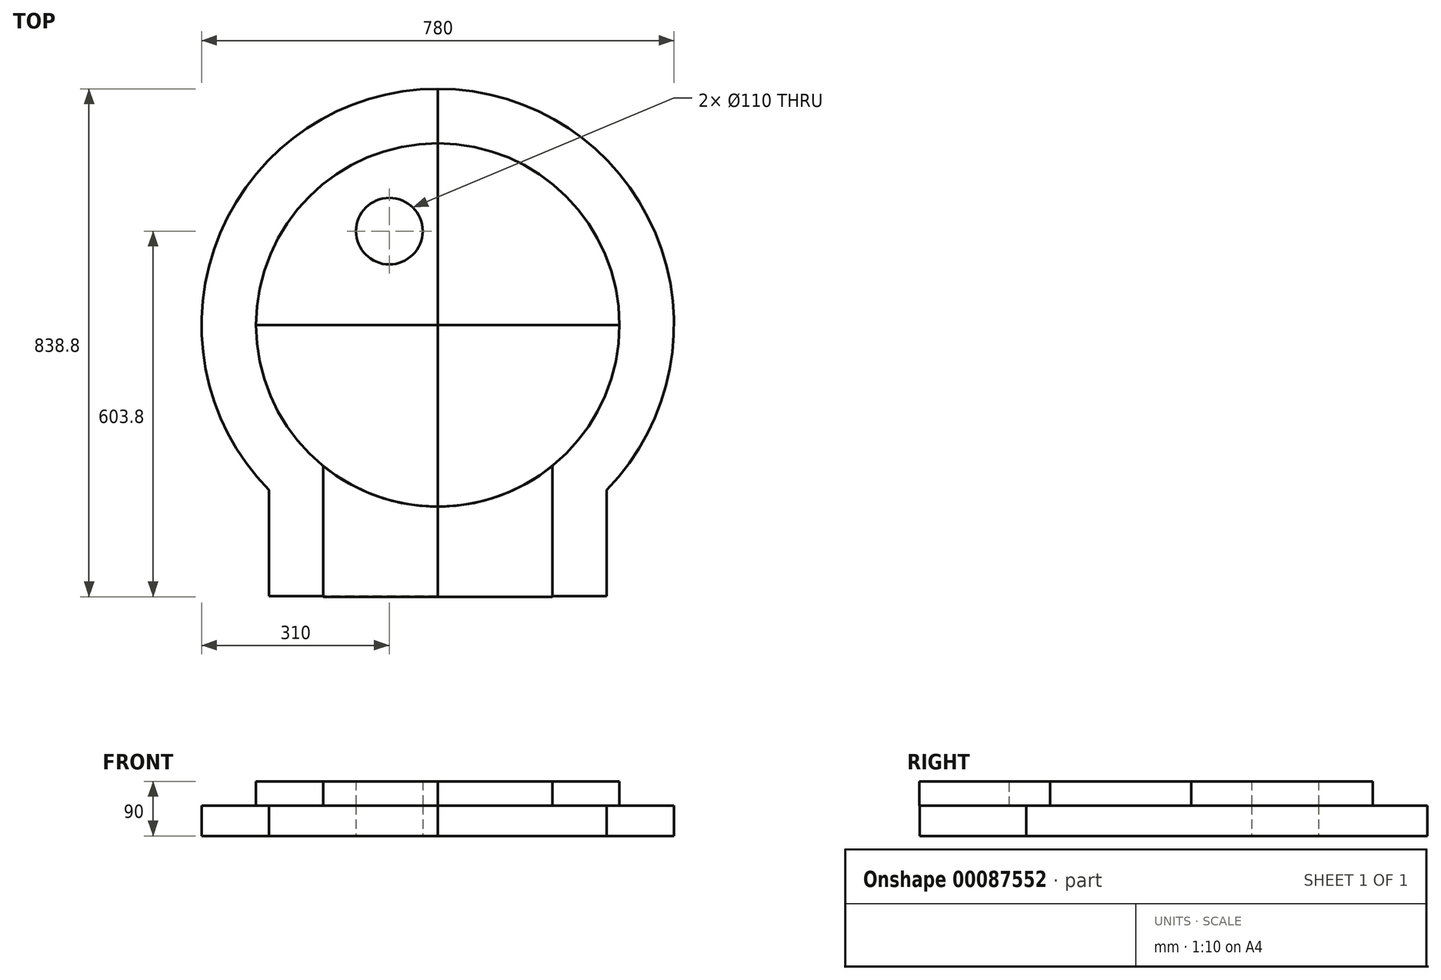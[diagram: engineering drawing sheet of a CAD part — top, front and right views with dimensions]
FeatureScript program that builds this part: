
annotation { "Feature Type Name" : "Feature", "Feature Type Description" : "" }
export const myFeature = defineFeature(function(context is Context, id is Id, definition is map)
    precondition{}
    {
        {
            var Q0;
            Q0=qCreatedBy(makeId("Front.planeOp"),FACE);
            var sketch = newSketch(context, id + "F0", { "sketchPlane" : qUnion([Q0])});
            skLineSegment(sketch, "E0", {"start": v(0, 0) * mm, "end": v(300, 0) * mm});
            skLineSegment(sketch, "E1", {"start": v(0, 0) * mm, "end": v(0, 40) * mm});
            skLineSegment(sketch, "E2", {"start": v(300, 0) * mm, "end": v(300, 40) * mm});
            skLineSegment(sketch, "E3", {"start": v(0, 40) * mm, "end": v(300, 40) * mm});
            skSolve(sketch);
        }
        {
            var Q0;
            Q0=makeQuery(id+"F0.imprint","IMPRINT",FACE,{"disambiguationData":[TD([[makeQuery(id+"F0.imprint","IMPRINT",EDGE,{"derivedFrom":sQuery(id+"F0.wireOp",EDGE,"E0")}),1.0]])]});
            var Q1;
            Q1=sQuery(id+"F0.wireOp",EDGE,"E1");
            revolve(context, id + "F1", {"entities" : qUnion([Q0]), "axis" : qUnion([Q1]), "revolveType" : RevolveType.ONE_DIRECTION, "angle" : 90 * degree});
        }
        {
            var Q0;
            Q0=makeQuery(id+"F1.opRevolve","SWEPT_BODY",BODY,{"disambiguationData":[OSD([sQuery(id+"F0.wireOp",EDGE,"E0"),sQuery(id+"F0.wireOp",EDGE,"E1"),sQuery(id+"F0.wireOp",EDGE,"E2"),sQuery(id+"F0.wireOp",EDGE,"E3")])]});
            var Q1;
            Q1=makeQuery(id+"F1.opRevolve","CAP_EDGE",EDGE,{"disambiguationData":[OSD([sQuery(id+"F0.wireOp",EDGE,"E1")])],"isStart":true});
            transform(context, id + "F2", {"entities" : qUnion([Q0]), "transformType" : TransformType.ROTATION, "transformAxis" : qUnion([Q1]), "angle" : 90 * degree, "makeCopy" : true});
        }
        {
            var Q0;
            Q0=makeQuery(id+"F2.opPattern","COPY",BODY,{"derivedFrom":makeQuery(id+"F1.opRevolve","SWEPT_BODY",BODY,{"disambiguationData":[OSD([sQuery(id+"F0.wireOp",EDGE,"E0"),sQuery(id+"F0.wireOp",EDGE,"E1"),sQuery(id+"F0.wireOp",EDGE,"E2"),sQuery(id+"F0.wireOp",EDGE,"E3")])]}),"instanceName":"1"});
            var Q1;
            Q1=makeQuery(id+"F1.opRevolve","CAP_EDGE",EDGE,{"disambiguationData":[OSD([sQuery(id+"F0.wireOp",EDGE,"E1")])],"isStart":true});
            transform(context, id + "F3", {"entities" : qUnion([Q0]), "transformType" : TransformType.ROTATION, "transformAxis" : qUnion([Q1]), "angle" : 90 * degree, "makeCopy" : true});
        }
        {
            var Q0;
            Q0=makeQuery(id+"F3.opPattern","COPY",BODY,{"derivedFrom":makeQuery(id+"F2.opPattern","COPY",BODY,{"derivedFrom":makeQuery(id+"F1.opRevolve","SWEPT_BODY",BODY,{"disambiguationData":[OSD([sQuery(id+"F0.wireOp",EDGE,"E0"),sQuery(id+"F0.wireOp",EDGE,"E1"),sQuery(id+"F0.wireOp",EDGE,"E2"),sQuery(id+"F0.wireOp",EDGE,"E3")])]}),"instanceName":"1"}),"instanceName":"1"});
            var Q1;
            Q1=makeQuery(id+"F1.opRevolve","CAP_EDGE",EDGE,{"disambiguationData":[OSD([sQuery(id+"F0.wireOp",EDGE,"E1")])],"isStart":true});
            transform(context, id + "F4", {"entities" : qUnion([Q0]), "transformType" : TransformType.ROTATION, "transformAxis" : qUnion([Q1]), "angle" : 90 * degree, "makeCopy" : true});
        }
        {
            var Q0;
            Q0=qCreatedBy(makeId("Right.planeOp"),FACE);
            var sketch = newSketch(context, id + "F5", { "sketchPlane" : qUnion([Q0])});
            skLineSegment(sketch, "E4", {"start": v(0, 0) * mm, "end": v(300, 0) * mm});
            skLineSegment(sketch, "E5", {"start": v(0, 0) * mm, "end": v(0, 40) * mm});
            skLineSegment(sketch, "E6", {"start": v(300, 0) * mm, "end": v(300, 40) * mm});
            skLineSegment(sketch, "E7", {"start": v(0, 40) * mm, "end": v(300, 40) * mm});
            skSolve(sketch);
        }
        {
            var Q0;
            Q0=makeQuery(id+"F5.imprint","IMPRINT",FACE,{"disambiguationData":[TD([[makeQuery(id+"F5.imprint","IMPRINT",EDGE,{"derivedFrom":sQuery(id+"F5.wireOp",EDGE,"E4")}),1.0]])]});
            extrude(context, id + "F6", {"entities" : qUnion([Q0]), "depth" : 189 * mm});
        }
        {
            var Q0;
            Q0=makeQuery(id+"F6.opExtrude","SWEPT_BODY",BODY,{"disambiguationData":[OSD([sQuery(id+"F5.wireOp",EDGE,"E4"),sQuery(id+"F5.wireOp",EDGE,"E5"),sQuery(id+"F5.wireOp",EDGE,"E6"),sQuery(id+"F5.wireOp",EDGE,"E7")])]});
            transform(context, id + "F7", {"entities" : qUnion([Q0]), "transformType" : TransformType.TRANSLATION_3D, "dx" : 0 * mm, "dy" : -448.8 * mm, "dz" : 0 * mm, "makeCopy" : false});
        }
        {
            var Q0;
            Q0=makeQuery(id+"F6.opExtrude","SWEPT_BODY",BODY,{"disambiguationData":[OSD([sQuery(id+"F5.wireOp",EDGE,"E4"),sQuery(id+"F5.wireOp",EDGE,"E5"),sQuery(id+"F5.wireOp",EDGE,"E6"),sQuery(id+"F5.wireOp",EDGE,"E7")])]});
            transform(context, id + "F8", {"entities" : qUnion([Q0]), "transformType" : TransformType.TRANSLATION_3D, "dx" : -189 * mm, "dy" : 0 * mm, "dz" : 0 * mm, "makeCopy" : true});
        }
        {
            var Q0;
            Q0=makeQuery(id+"F3.opPattern","COPY",BODY,{"derivedFrom":makeQuery(id+"F2.opPattern","COPY",BODY,{"derivedFrom":makeQuery(id+"F1.opRevolve","SWEPT_BODY",BODY,{"disambiguationData":[OSD([sQuery(id+"F0.wireOp",EDGE,"E0"),sQuery(id+"F0.wireOp",EDGE,"E1"),sQuery(id+"F0.wireOp",EDGE,"E2"),sQuery(id+"F0.wireOp",EDGE,"E3")])]}),"instanceName":"1"}),"instanceName":"1"});
            var Q1;
            Q1=makeQuery(id+"F8.opPattern","COPY",BODY,{"derivedFrom":makeQuery(id+"F6.opExtrude","SWEPT_BODY",BODY,{"disambiguationData":[OSD([sQuery(id+"F5.wireOp",EDGE,"E4"),sQuery(id+"F5.wireOp",EDGE,"E5"),sQuery(id+"F5.wireOp",EDGE,"E6"),sQuery(id+"F5.wireOp",EDGE,"E7")])]}),"instanceName":"1"});
            booleanBodies(context, id + "F9", {"operationType" : BooleanOperationType.SUBTRACTION, "tools" : qUnion([Q0]), "targets" : qUnion([Q1]), "keepTools" : true});
        }
        {
            var Q0;
            Q0=makeQuery(id+"F4.opPattern","COPY",BODY,{"derivedFrom":makeQuery(id+"F3.opPattern","COPY",BODY,{"derivedFrom":makeQuery(id+"F2.opPattern","COPY",BODY,{"derivedFrom":makeQuery(id+"F1.opRevolve","SWEPT_BODY",BODY,{"disambiguationData":[OSD([sQuery(id+"F0.wireOp",EDGE,"E0"),sQuery(id+"F0.wireOp",EDGE,"E1"),sQuery(id+"F0.wireOp",EDGE,"E2"),sQuery(id+"F0.wireOp",EDGE,"E3")])]}),"instanceName":"1"}),"instanceName":"1"}),"instanceName":"1"});
            var Q1;
            Q1=makeQuery(id+"F6.opExtrude","SWEPT_BODY",BODY,{"disambiguationData":[OSD([sQuery(id+"F5.wireOp",EDGE,"E4"),sQuery(id+"F5.wireOp",EDGE,"E5"),sQuery(id+"F5.wireOp",EDGE,"E6"),sQuery(id+"F5.wireOp",EDGE,"E7")])]});
            booleanBodies(context, id + "F10", {"operationType" : BooleanOperationType.SUBTRACTION, "tools" : qUnion([Q0]), "targets" : qUnion([Q1]), "keepTools" : true});
        }
        {
            var Q0;
            Q0=qCreatedBy(makeId("Top.planeOp"),FACE);
            var sketch = newSketch(context, id + "F11", { "sketchPlane" : qUnion([Q0])});
            skLineSegment(sketch, "E8", {"start": v(0, 0) * mm, "end": v(410, 0) * mm});
            skLineSegment(sketch, "E9", {"start": v(410, 0) * mm, "end": v(410, 450) * mm});
            skLineSegment(sketch, "E10", {"start": v(0, 0) * mm, "end": v(-410, 0) * mm});
            skLineSegment(sketch, "E11", {"start": v(-410, 0) * mm, "end": v(-410, -410) * mm});
            skLineSegment(sketch, "E12", {"start": v(0, 0) * mm, "end": v(0, -410) * mm});
            skLineSegment(sketch, "E13", {"start": v(0, 0) * mm, "end": v(0, 450) * mm});
            skLineSegment(sketch, "E14.bottom", {"start": v(-410, -410) * mm, "end": v(0, -410) * mm});
            skLineSegment(sketch, "E14.top", {"start": v(-410, 450) * mm, "end": v(0, 450) * mm});
            skLineSegment(sketch, "E14.right", {"start": v(0, -410) * mm, "end": v(0, 450) * mm});
            skLineSegment(sketch, "E15.bottom", {"start": v(0, -410) * mm, "end": v(410, -410) * mm});
            skLineSegment(sketch, "E15.top", {"start": v(0, 450) * mm, "end": v(410, 450) * mm});
            skLineSegment(sketch, "E16", {"start": v(-410, 0) * mm, "end": v(-410, 450) * mm});
            skLineSegment(sketch, "E17", {"start": v(410, 0) * mm, "end": v(410, -410) * mm});
            skSolve(sketch);
        }
        {
            var Q0;
            {var subQ0=sQuery(id+"F11.wireOp",EDGE,"E8");Q0=makeQuery(id+"F11.imprint","IMPRINT",FACE,{"disambiguationData":[TD([[makeQuery(id+"F11.imprint","IMPRINT",EDGE,{"derivedFrom":subQ0}),-1.0]])]});}
            var Q1;
            {var subQ0=sQuery(id+"F11.wireOp",EDGE,"E8");Q1=makeQuery(id+"F11.imprint","IMPRINT",FACE,{"disambiguationData":[TD([[makeQuery(id+"F11.imprint","IMPRINT",EDGE,{"derivedFrom":subQ0}),1.0]])]});}
            var Q2;
            {var subQ0=sQuery(id+"F11.wireOp",EDGE,"E10");Q2=makeQuery(id+"F11.imprint","IMPRINT",FACE,{"disambiguationData":[TD([[makeQuery(id+"F11.imprint","IMPRINT",EDGE,{"derivedFrom":subQ0}),-1.0]])]});}
            var Q3;
            {var subQ0=sQuery(id+"F11.wireOp",EDGE,"E10");Q3=makeQuery(id+"F11.imprint","IMPRINT",FACE,{"disambiguationData":[TD([[makeQuery(id+"F11.imprint","IMPRINT",EDGE,{"derivedFrom":subQ0}),1.0]])]});}
            extrude(context, id + "F12", {"entities" : qUnion([Q0, Q1, Q2, Q3]), "depth" : 50 * mm});
        }
        {
            var Q0;
            Q0=makeQuery(id+"F12.opExtrude","SWEPT_BODY",BODY,{"disambiguationData":[OSD([sQuery(id+"F11.wireOp",EDGE,"E14.bottom"),sQuery(id+"F11.wireOp",EDGE,"E14.top"),sQuery(id+"F11.wireOp",EDGE,"E14.left"),sQuery(id+"F11.wireOp",EDGE,"E15.bottom"),sQuery(id+"F11.wireOp",EDGE,"E15.top"),sQuery(id+"F11.wireOp",EDGE,"E15.right")])]});
            transform(context, id + "F13", {"entities" : qUnion([Q0]), "transformType" : TransformType.TRANSLATION_3D, "dx" : 0 * mm, "dy" : 0 * mm, "dz" : -50 * mm, "makeCopy" : false});
        }
        {
            var Q0;
            Q0=makeQuery(id+"F12.opExtrude","SWEPT_BODY",BODY,{"disambiguationData":[OSD([sQuery(id+"F11.wireOp",EDGE,"E9"),sQuery(id+"F11.wireOp",EDGE,"E11"),sQuery(id+"F11.wireOp",EDGE,"E14.bottom"),sQuery(id+"F11.wireOp",EDGE,"E14.top"),sQuery(id+"F11.wireOp",EDGE,"E15.bottom"),sQuery(id+"F11.wireOp",EDGE,"E15.top"),sQuery(id+"F11.wireOp",EDGE,"E16"),sQuery(id+"F11.wireOp",EDGE,"E17")])]});
            transform(context, id + "F14", {"entities" : qUnion([Q0]), "transformType" : TransformType.TRANSLATION_3D, "dx" : 0 * mm, "dy" : -40 * mm, "dz" : 0 * mm, "makeCopy" : false});
        }
        {
            var Q0;
            Q0=makeQuery(id+"F3.opPattern","COPY",BODY,{"derivedFrom":makeQuery(id+"F2.opPattern","COPY",BODY,{"derivedFrom":makeQuery(id+"F1.opRevolve","SWEPT_BODY",BODY,{"disambiguationData":[OSD([sQuery(id+"F0.wireOp",EDGE,"E0"),sQuery(id+"F0.wireOp",EDGE,"E1"),sQuery(id+"F0.wireOp",EDGE,"E2"),sQuery(id+"F0.wireOp",EDGE,"E3")])]}),"instanceName":"1"}),"instanceName":"1"});
            var Q1;
            Q1=makeQuery(id+"F2.opPattern","COPY",BODY,{"derivedFrom":makeQuery(id+"F1.opRevolve","SWEPT_BODY",BODY,{"disambiguationData":[OSD([sQuery(id+"F0.wireOp",EDGE,"E0"),sQuery(id+"F0.wireOp",EDGE,"E1"),sQuery(id+"F0.wireOp",EDGE,"E2"),sQuery(id+"F0.wireOp",EDGE,"E3")])]}),"instanceName":"1"});
            var Q2;
            Q2=makeQuery(id+"F4.opPattern","COPY",BODY,{"derivedFrom":makeQuery(id+"F3.opPattern","COPY",BODY,{"derivedFrom":makeQuery(id+"F2.opPattern","COPY",BODY,{"derivedFrom":makeQuery(id+"F1.opRevolve","SWEPT_BODY",BODY,{"disambiguationData":[OSD([sQuery(id+"F0.wireOp",EDGE,"E0"),sQuery(id+"F0.wireOp",EDGE,"E1"),sQuery(id+"F0.wireOp",EDGE,"E2"),sQuery(id+"F0.wireOp",EDGE,"E3")])]}),"instanceName":"1"}),"instanceName":"1"}),"instanceName":"1"});
            var Q3;
            Q3=makeQuery(id+"F6.opExtrude","SWEPT_BODY",BODY,{"disambiguationData":[OSD([sQuery(id+"F5.wireOp",EDGE,"E4"),sQuery(id+"F5.wireOp",EDGE,"E5"),sQuery(id+"F5.wireOp",EDGE,"E6"),sQuery(id+"F5.wireOp",EDGE,"E7")])]});
            var Q4;
            Q4=makeQuery(id+"F8.opPattern","COPY",BODY,{"derivedFrom":makeQuery(id+"F6.opExtrude","SWEPT_BODY",BODY,{"disambiguationData":[OSD([sQuery(id+"F5.wireOp",EDGE,"E4"),sQuery(id+"F5.wireOp",EDGE,"E5"),sQuery(id+"F5.wireOp",EDGE,"E6"),sQuery(id+"F5.wireOp",EDGE,"E7")])]}),"instanceName":"1"});
            var Q5;
            Q5=makeQuery(id+"F12.opExtrude","SWEPT_BODY",BODY,{"disambiguationData":[OSD([sQuery(id+"F11.wireOp",EDGE,"E9"),sQuery(id+"F11.wireOp",EDGE,"E11"),sQuery(id+"F11.wireOp",EDGE,"E14.bottom"),sQuery(id+"F11.wireOp",EDGE,"E14.top"),sQuery(id+"F11.wireOp",EDGE,"E15.bottom"),sQuery(id+"F11.wireOp",EDGE,"E15.top"),sQuery(id+"F11.wireOp",EDGE,"E16"),sQuery(id+"F11.wireOp",EDGE,"E17")])]});
            var Q6;
            Q6=makeQuery(id+"F1.opRevolve","SWEPT_BODY",BODY,{"disambiguationData":[OSD([sQuery(id+"F0.wireOp",EDGE,"E0"),sQuery(id+"F0.wireOp",EDGE,"E1"),sQuery(id+"F0.wireOp",EDGE,"E2"),sQuery(id+"F0.wireOp",EDGE,"E3")])]});
            transform(context, id + "F15", {"entities" : qUnion([Q0, Q1, Q2, Q3, Q4, Q5, Q6]), "transformType" : TransformType.TRANSLATION_3D, "dx" : 0 * mm, "dy" : 20 * mm, "dz" : -50 * mm, "makeCopy" : false});
        }
        {
            var Q0;
            Q0=qCreatedBy(makeId("Top.planeOp"),FACE);
            var sketch = newSketch(context, id + "F16", { "sketchPlane" : qUnion([Q0])});
            skLineSegment(sketch, "E18", {"start": v(0, 0) * mm, "end": v(0, 20) * mm});
            skLineSegment(sketch, "E19", {"start": v(0, 20) * mm, "end": v(0, 410) * mm});
            skLineSegment(sketch, "E20", {"start": v(0, 20) * mm, "end": v(0, -428) * mm});
            skLineSegment(sketch, "E21", {"start": v(0, -428) * mm, "end": v(-279, -428) * mm});
            skLineSegment(sketch, "E22", {"start": v(-279, -428) * mm, "end": v(-279, -252.5) * mm});
            skArc(sketch, "E23", {"start": v(-279, -252.5) * mm, "mid": v(-359.43, 171.37) * mm, "end": v(0, 410) * mm});
            skSolve(sketch);
        }
        {
            var Q0;
            {var subQ1=sQuery(id+"F16.wireOp",EDGE,"E19");Q0=makeQuery(id+"F16.imprint","IMPRINT",FACE,{"disambiguationData":[TD([[makeQuery(id+"F16.imprint","IMPRINT",EDGE,{"derivedFrom":subQ1}),1.0]])]});}
            extrude(context, id + "F17", {"entities" : qUnion([Q0]), "depth" : 50 * mm});
        }
        {
            var Q0;
            Q0=makeQuery(id+"F17.opExtrude","SWEPT_BODY",BODY,{"disambiguationData":[OSD([sQuery(id+"F16.wireOp",EDGE,"E19"),sQuery(id+"F16.wireOp",EDGE,"E20"),sQuery(id+"F16.wireOp",EDGE,"E21"),sQuery(id+"F16.wireOp",EDGE,"E22"),sQuery(id+"F16.wireOp",EDGE,"E23")])]});
            transform(context, id + "F18", {"entities" : qUnion([Q0]), "transformType" : TransformType.TRANSLATION_3D, "dx" : 0 * mm, "dy" : 0 * mm, "dz" : -100 * mm, "makeCopy" : false});
        }
        {
            var Q0;
            Q0=makeQuery(id+"F17.opExtrude","SWEPT_BODY",BODY,{"disambiguationData":[OSD([sQuery(id+"F16.wireOp",EDGE,"E19"),sQuery(id+"F16.wireOp",EDGE,"E20"),sQuery(id+"F16.wireOp",EDGE,"E21"),sQuery(id+"F16.wireOp",EDGE,"E22"),sQuery(id+"F16.wireOp",EDGE,"E23")])]});
            var Q1;
            Q1=makeQuery(id+"F17.opExtrude","CAP_EDGE",EDGE,{"disambiguationData":[OSD([sQuery(id+"F16.wireOp",EDGE,"E19"),sQuery(id+"F16.wireOp",EDGE,"E20")])],"isStart":false});
            transform(context, id + "F19", {"entities" : qUnion([Q0]), "transformType" : TransformType.ROTATION, "transformAxis" : qUnion([Q1]), "angle" : 180 * degree, "makeCopy" : true});
        }
        {
            var Q0;
            Q0=makeQuery(id+"F19.opPattern","COPY",BODY,{"derivedFrom":makeQuery(id+"F17.opExtrude","SWEPT_BODY",BODY,{"disambiguationData":[OSD([sQuery(id+"F16.wireOp",EDGE,"E19"),sQuery(id+"F16.wireOp",EDGE,"E20"),sQuery(id+"F16.wireOp",EDGE,"E21"),sQuery(id+"F16.wireOp",EDGE,"E22"),sQuery(id+"F16.wireOp",EDGE,"E23")])]}),"instanceName":"1"});
            transform(context, id + "F20", {"entities" : qUnion([Q0]), "transformType" : TransformType.TRANSLATION_3D, "dx" : 0 * mm, "dy" : 0 * mm, "dz" : -50 * mm, "makeCopy" : false});
        }
        {
            var Q0;
            Q0=makeQuery(id+"F12.opExtrude","SWEPT_BODY",BODY,{"disambiguationData":[OSD([sQuery(id+"F11.wireOp",EDGE,"E9"),sQuery(id+"F11.wireOp",EDGE,"E11"),sQuery(id+"F11.wireOp",EDGE,"E14.bottom"),sQuery(id+"F11.wireOp",EDGE,"E14.top"),sQuery(id+"F11.wireOp",EDGE,"E15.bottom"),sQuery(id+"F11.wireOp",EDGE,"E15.top"),sQuery(id+"F11.wireOp",EDGE,"E16"),sQuery(id+"F11.wireOp",EDGE,"E17")])]});
            deleteBodies(context, id + "F21", {"entities" : qUnion([Q0])});
        }
        {
            var Q0;
            Q0=qCreatedBy(makeId("Top.planeOp"),FACE);
            var sketch = newSketch(context, id + "F22", { "sketchPlane" : qUnion([Q0])});
            skLineSegment(sketch, "E24", {"start": v(0, 0) * mm, "end": v(0, 20) * mm});
            skLineSegment(sketch, "E25", {"start": v(0, 20) * mm, "end": v(0, 120) * mm});
            skLineSegment(sketch, "E26", {"start": v(-80, 120) * mm, "end": v(-80, 175) * mm});
            skCircle(sketch, "E27", {"center": v(-80, 175) * mm, "radius": 55 * mm});
            skLineSegment(sketch, "E28", {"start": v(0, 120) * mm, "end": v(-80, 120) * mm});
            skSolve(sketch);
        }
        {
            var Q0;
            Q0=makeQuery(id+"F22.imprint","IMPRINT",FACE,{"disambiguationData":[TD([[makeQuery(id+"F22.imprint","IMPRINT",EDGE,{"derivedFrom":sQuery(id+"F22.wireOp",EDGE,"E27")}),1.0]])]});
            extrude(context, id + "F23", {"entities" : qUnion([Q0]), "depth" : 200 * mm});
        }
        {
            var Q0;
            Q0=makeQuery(id+"F23.opExtrude","SWEPT_BODY",BODY,{"disambiguationData":[OSD([sQuery(id+"F22.wireOp",EDGE,"E27")])]});
            transform(context, id + "F24", {"entities" : qUnion([Q0]), "transformType" : TransformType.TRANSLATION_3D, "dx" : 0 * mm, "dy" : 0 * mm, "dz" : -200 * mm, "makeCopy" : false});
        }
        {
            var Q0;
            Q0=makeQuery(id+"F23.opExtrude","SWEPT_BODY",BODY,{"disambiguationData":[OSD([sQuery(id+"F22.wireOp",EDGE,"E27")])]});
            var Q1;
            Q1=makeQuery(id+"F2.opPattern","COPY",BODY,{"derivedFrom":makeQuery(id+"F1.opRevolve","SWEPT_BODY",BODY,{"disambiguationData":[OSD([sQuery(id+"F0.wireOp",EDGE,"E0"),sQuery(id+"F0.wireOp",EDGE,"E1"),sQuery(id+"F0.wireOp",EDGE,"E2"),sQuery(id+"F0.wireOp",EDGE,"E3")])]}),"instanceName":"1"});
            var Q2;
            Q2=makeQuery(id+"F17.opExtrude","SWEPT_BODY",BODY,{"disambiguationData":[OSD([sQuery(id+"F16.wireOp",EDGE,"E19"),sQuery(id+"F16.wireOp",EDGE,"E20"),sQuery(id+"F16.wireOp",EDGE,"E21"),sQuery(id+"F16.wireOp",EDGE,"E22"),sQuery(id+"F16.wireOp",EDGE,"E23")])]});
            booleanBodies(context, id + "F25", {"operationType" : BooleanOperationType.SUBTRACTION, "tools" : qUnion([Q0]), "targets" : qUnion([Q1, Q2])});
        }
        {
            var Q0;
            Q0=makeQuery(id+"F6.opExtrude","SWEPT_BODY",BODY,{"disambiguationData":[OSD([sQuery(id+"F5.wireOp",EDGE,"E4"),sQuery(id+"F5.wireOp",EDGE,"E5"),sQuery(id+"F5.wireOp",EDGE,"E6"),sQuery(id+"F5.wireOp",EDGE,"E7")])]});
            var Q1;
            Q1=makeQuery(id+"F8.opPattern","COPY",BODY,{"derivedFrom":makeQuery(id+"F6.opExtrude","SWEPT_BODY",BODY,{"disambiguationData":[OSD([sQuery(id+"F5.wireOp",EDGE,"E4"),sQuery(id+"F5.wireOp",EDGE,"E5"),sQuery(id+"F5.wireOp",EDGE,"E6"),sQuery(id+"F5.wireOp",EDGE,"E7")])]}),"instanceName":"1"});
            var Q2;
            Q2=makeQuery(id+"F17.opExtrude","SWEPT_BODY",BODY,{"disambiguationData":[OSD([sQuery(id+"F16.wireOp",EDGE,"E19"),sQuery(id+"F16.wireOp",EDGE,"E20"),sQuery(id+"F16.wireOp",EDGE,"E21"),sQuery(id+"F16.wireOp",EDGE,"E22"),sQuery(id+"F16.wireOp",EDGE,"E23")])]});
            var Q3;
            Q3=makeQuery(id+"F19.opPattern","COPY",BODY,{"derivedFrom":makeQuery(id+"F17.opExtrude","SWEPT_BODY",BODY,{"disambiguationData":[OSD([sQuery(id+"F16.wireOp",EDGE,"E19"),sQuery(id+"F16.wireOp",EDGE,"E20"),sQuery(id+"F16.wireOp",EDGE,"E21"),sQuery(id+"F16.wireOp",EDGE,"E22"),sQuery(id+"F16.wireOp",EDGE,"E23")])]}),"instanceName":"1"});
            var Q4;
            Q4=makeQuery(id+"F1.opRevolve","SWEPT_BODY",BODY,{"disambiguationData":[OSD([sQuery(id+"F0.wireOp",EDGE,"E0"),sQuery(id+"F0.wireOp",EDGE,"E1"),sQuery(id+"F0.wireOp",EDGE,"E2"),sQuery(id+"F0.wireOp",EDGE,"E3")])]});
            var Q5;
            Q5=makeQuery(id+"F2.opPattern","COPY",BODY,{"derivedFrom":makeQuery(id+"F1.opRevolve","SWEPT_BODY",BODY,{"disambiguationData":[OSD([sQuery(id+"F0.wireOp",EDGE,"E0"),sQuery(id+"F0.wireOp",EDGE,"E1"),sQuery(id+"F0.wireOp",EDGE,"E2"),sQuery(id+"F0.wireOp",EDGE,"E3")])]}),"instanceName":"1"});
            var Q6;
            Q6=makeQuery(id+"F4.opPattern","COPY",BODY,{"derivedFrom":makeQuery(id+"F3.opPattern","COPY",BODY,{"derivedFrom":makeQuery(id+"F2.opPattern","COPY",BODY,{"derivedFrom":makeQuery(id+"F1.opRevolve","SWEPT_BODY",BODY,{"disambiguationData":[OSD([sQuery(id+"F0.wireOp",EDGE,"E0"),sQuery(id+"F0.wireOp",EDGE,"E1"),sQuery(id+"F0.wireOp",EDGE,"E2"),sQuery(id+"F0.wireOp",EDGE,"E3")])]}),"instanceName":"1"}),"instanceName":"1"}),"instanceName":"1"});
            var Q7;
            Q7=makeQuery(id+"F3.opPattern","COPY",BODY,{"derivedFrom":makeQuery(id+"F2.opPattern","COPY",BODY,{"derivedFrom":makeQuery(id+"F1.opRevolve","SWEPT_BODY",BODY,{"disambiguationData":[OSD([sQuery(id+"F0.wireOp",EDGE,"E0"),sQuery(id+"F0.wireOp",EDGE,"E1"),sQuery(id+"F0.wireOp",EDGE,"E2"),sQuery(id+"F0.wireOp",EDGE,"E3")])]}),"instanceName":"1"}),"instanceName":"1"});
            transform(context, id + "F26", {"entities" : qUnion([Q0, Q1, Q2, Q3, Q4, Q5, Q6, Q7]), "transformType" : TransformType.TRANSLATION_3D, "dx" : 0 * mm, "dy" : 0 * mm, "dz" : 3 * mm, "makeCopy" : false});
        }
    });
